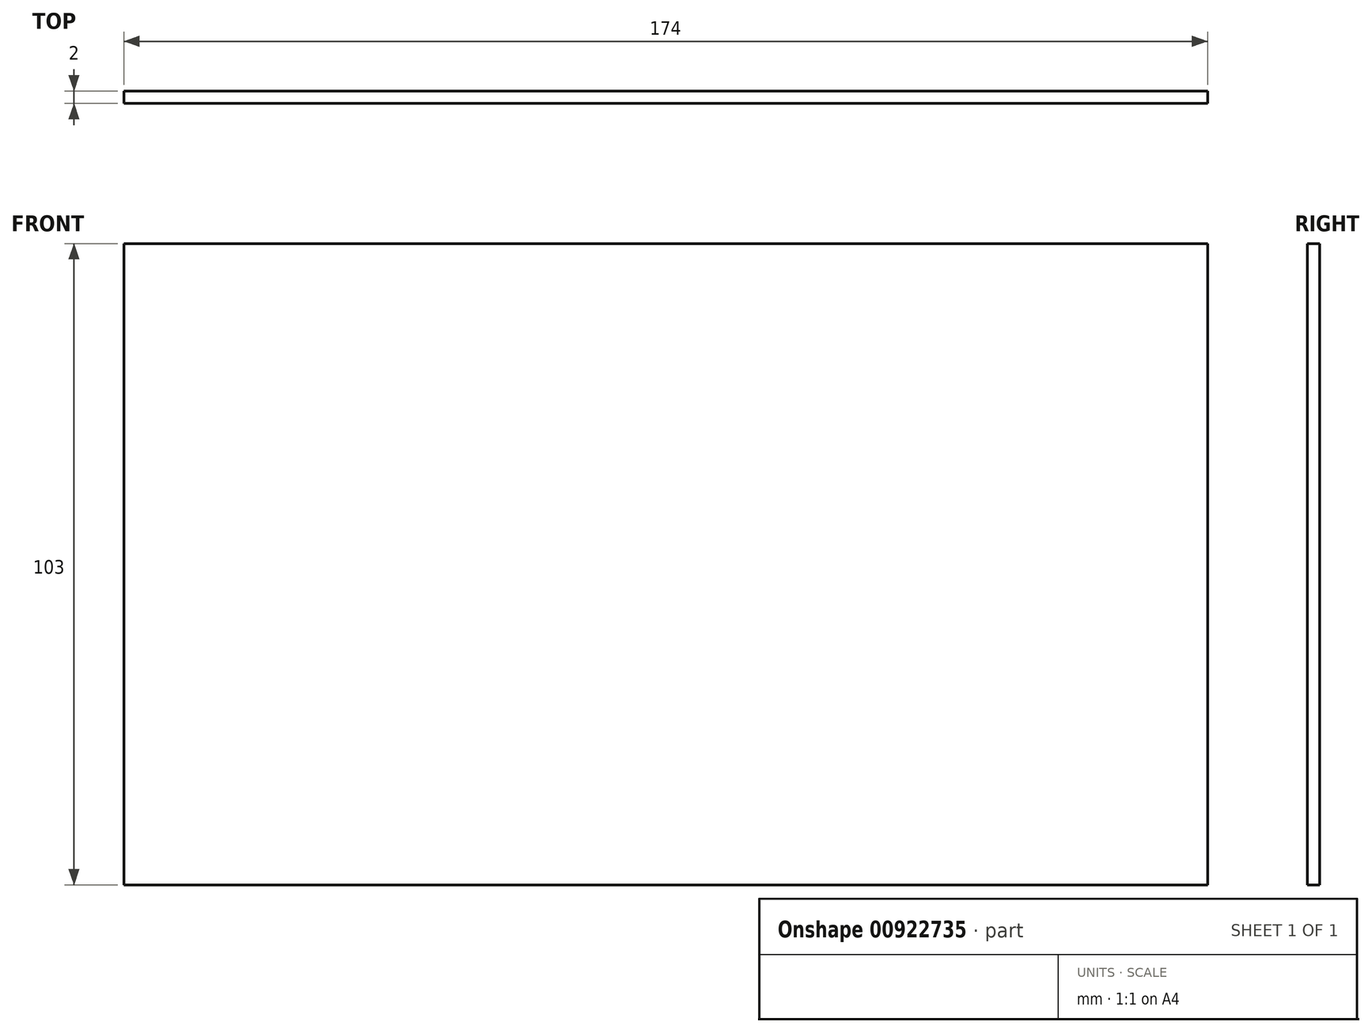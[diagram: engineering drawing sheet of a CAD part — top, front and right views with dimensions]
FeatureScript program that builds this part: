
annotation { "Feature Type Name" : "Feature", "Feature Type Description" : "" }
export const myFeature = defineFeature(function(context is Context, id is Id, definition is map)
    precondition{}
    {
        {
            var Q0;
            Q0=qCreatedBy(makeId("Front.planeOp"),FACE);
            var sketch = newSketch(context, id + "F0", { "sketchPlane" : qUnion([Q0])});
            skLineSegment(sketch, "E0.bottom", {"start": v(87, -51.5) * mm, "end": v(-87, -51.5) * mm});
            skLineSegment(sketch, "E0.top", {"start": v(87, 51.5) * mm, "end": v(-87, 51.5) * mm});
            skLineSegment(sketch, "E0.left", {"start": v(87, -51.5) * mm, "end": v(87, 51.5) * mm});
            skLineSegment(sketch, "E0.right", {"start": v(-87, -51.5) * mm, "end": v(-87, 51.5) * mm});
            skPoint(sketch, "E0.middle", {"position": v(0, 0) * mm});
            skSolve(sketch);
        }
        {
            var Q0;
            Q0 = qSketchRegion(id + "F0", true);
            extrude(context, id + "F1", {"entities" : qUnion([Q0]), "endBound" : BoundingType.SYMMETRIC, "depth" : 2 * mm, "offsetDistance" : 25 * mm});
        }
    });
